# Revit family: 55442103(2022)
name_source: partatom
category: Plumbing Fixtures
units: mm (PartAtom-declared; Revit-internal decimal feet)

## family parameters
Always vertical = Yes
Cut with Voids When Loaded = No
OmniClass Number = 23.45.55.00
OmniClass Title = Sanitary Faucets, Wastes
Part Type = Normal
Room Calculation Point = No
Round Connector Dimension = Use Diameter
Shared = No
Work Plane-Based = No

## types (1)
- 55442103 Bath and shower faucet
    2D/3D/BIM Files URL = http://static.hansa.com
    Aerator = Standard aerator
    Approval DVGW = DW-6506DO0165
    AssetType = Fixed
    BIMObjectName = 55442103(2022)
    Backflow Prevention EN1717 = EB
    BodyMaterial = Brass
    Brand = HANSA
    Catalog Drawing URL = http://static.hansa.com
    Category = Bathtub & Shower
    CloseOffRating = 0
    Color = Chrome
    Connection = Eccentric coupling(s)
    Connection Size = G3/4
    Default Elevation = 0 mm  [stored 0 ft]
    Dimension Drawing URL = http://static.hansa.com
    Diverter = Pull operated diverter;Automatic reset
    DurationUnit = Year
    EAN Number = 4057304019067
    EN Standard = EN 817
    ETIM Class Number = EC010862 Bath mixing tap
    FDV Document URL = http://www.hansa.com
    FaucetMainMaterial = Brass
    Features = Single-lever
    Finish = Polished
    Flow Drawing URL = http://static.hansa.com
    Flow Rate At 300kPa = 0.4 L/s
    FlowCoefficient = 0
    Group = Bath and shower faucet
    IfcExportAs = IfcValveType
    IfcExportType = FAUCET
    Installation Type = Wall mounted
    Installation Width = CC150 ± 15 mm
    Installation and Maintenance Guide URL = http://static.hansa.com
    Lever Handle = Hot/Cold symbols;Single operating lever/handle
    Manufacturer = HANSA
    ManufacturerName = HANSA
    ManufacturerURL = http://www.hansa.com
    Market = Austria;Czech Republic;Germany;International;Italy;Slovakia
    Material = Brass
    Max. Hot Water Supply = 80 °C
    Mechanical Parts = ø 35 mm ceramic cartridge for flow and temperature control
    Mobile Product Information URL = http://mpi.hansa.com
    Model = 55442103 Bath and shower faucet
    ModelReference = 55442103
    NBSDescription = Shower mixers
    NBSReference = 45-35-70/335
    Name = 55442103 Bath and shower faucet
    Name_en = 55442103 Bath and shower faucet
    Noise Class = I (ISO 3822)
    NominalDepth = 186 mm
    NominalHeight = 111 mm
    NominalWidth = 219 mm
    Product Code = 55442103
    Product Family = 5160
    Product Image URL = http://static.hansa.com
    Product URL = http://static.hansa.com
    Sales Package dimensions (LxWxH) = 245 x 195 x 120
    Shape = Sculptured
    Size = 220x185x110 mm
    Spare-Part Information URL = http://static.hansa.com
    Spout Projection = 165 mm
    Spout Type = Fixed spout
    Surface treatment = Chrome
    Technical DataSheet URL = http://www.hansa.com
    Temperature = THERMO COOL
    UNSPSC Class Number = 30181700 Faucets or taps
    URL DVGW = http://static.hansa.com
    URL Declaration Of Performance (DOP) = http://static.hansa.com
    URL Declaration of Asbestos = http://static.hansa.com
    URL Declaration of Conformity = http://static.hansa.com
    URL Declaration of SCIP = http://static.hansa.com
    URL EU Packaging Declaration = http://static.hansa.com
    URL EcoLabel Declaration = http://static.hansa.com
    URL REACH = http://static.hansa.com
    URL UWL = http://static.hansa.com
    Uniclass2 = Pr_40_30_96_78
    Uniclass2015Description = Shower manual water supply sets
    Uniclass2015Reference = Pr_40_20_87_78
    Version = 1
    VersionDate = 01/06/2023
    Warranty Information URL = http://warranty.hansa.com
    WarrantyDescription = http://warranty.hansa.com
    WarrantyDurationUnit = Year
    Working Pressure = 50 - 1000 kPa

note: [stored X ft] marks values corroborated as IEEE doubles in the binary element streams (Revit-internal decimal feet)

## geometry (parser evidence)
native form markers: Sweep x6
no freeform markers — native parametric forms only
